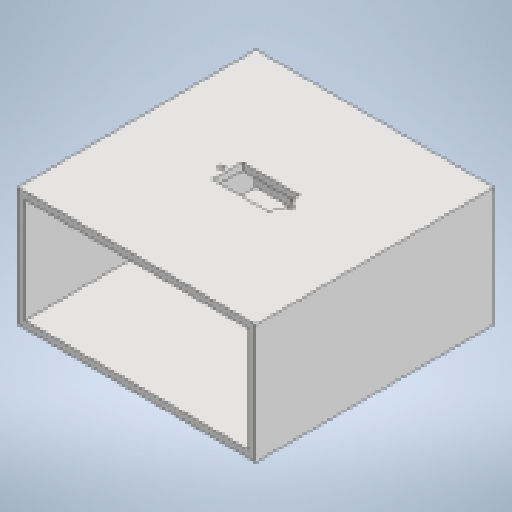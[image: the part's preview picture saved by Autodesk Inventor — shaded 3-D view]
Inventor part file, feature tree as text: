
AUTODESK INVENTOR PART (.ipt)
format: ipt  version: 2023 (Build 270158000, 158)  size: 151,552 bytes
history: native  units: mm
features: extrude x3, sketch x3, other x1, shell x1, projected_geometry x1
ambient origin geometry x8: Origin, YZ Plane, XZ Plane, XY Plane, X Axis, Y Axis, Z Axis, Center Point
bodies: Body1 (feature_tree)
feature tree (9):
  other  "實體1"
  extrude  "擠出1"  Depth=100.0mm
  shell  "薄殼1"  Thickness=100.0mm
  extrude  "擠出2"  Depth=50.0mm TaperAngle=0.0deg
  extrude  "擠出3"  Depth=3.0mm
  sketch  "草圖1"
  sketch  "草圖2"
  projected_geometry  "投影迴路1"
  sketch  "草圖3"
